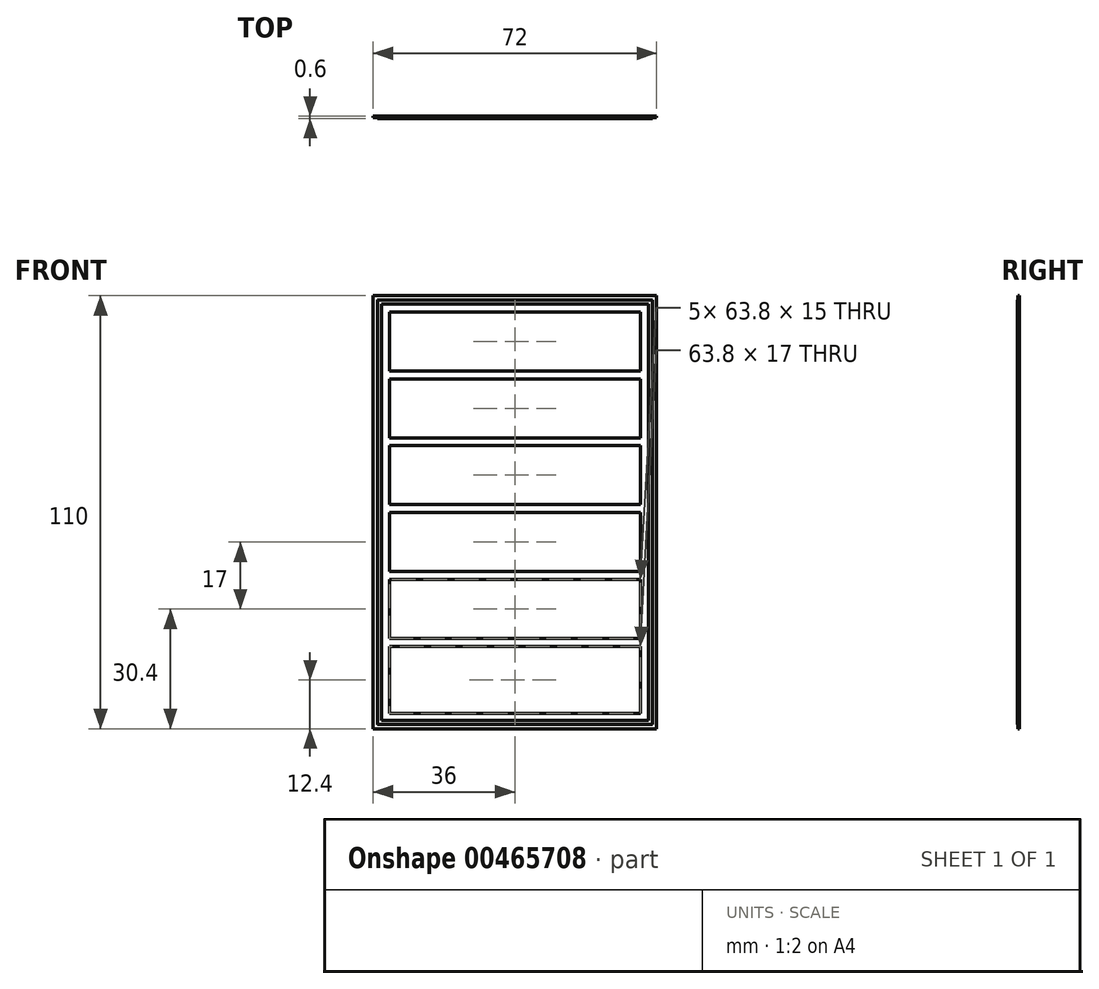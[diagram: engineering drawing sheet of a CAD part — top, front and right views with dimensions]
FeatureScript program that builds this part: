
annotation { "Feature Type Name" : "Feature", "Feature Type Description" : "" }
export const myFeature = defineFeature(function(context is Context, id is Id, definition is map)
    precondition{}
    {
        {
            var Q0;
            Q0=qCreatedBy(makeId("Top.planeOp"),FACE);
            var sketch = newSketch(context, id + "F0", { "sketchPlane" : qUnion([Q0])});
            skLineSegment(sketch, "E0.bottom", {"start": v(36, 0.05) * mm, "end": v(-36, 0.05) * mm});
            skLineSegment(sketch, "E0.top", {"start": v(36, -0.05) * mm, "end": v(-36, -0.05) * mm});
            skLineSegment(sketch, "E0.left", {"start": v(36, 0.05) * mm, "end": v(36, -0.05) * mm});
            skLineSegment(sketch, "E0.right", {"start": v(-36, 0.05) * mm, "end": v(-36, -0.05) * mm});
            skPoint(sketch, "E0.middle", {"position": v(0, 0) * mm});
            skSolve(sketch);
        }
        {
            var Q0;
            Q0 = qSketchRegion(id + "F0", true);
            extrude(context, id + "F1", {"entities" : qUnion([Q0]), "depth" : 110 * mm});
        }
        {
            var Q0;
            Q0=makeQuery(id+"F1.opExtrude","SWEPT_FACE",FACE,{"disambiguationData":[OSD([sQuery(id+"F0.wireOp",EDGE,"E0.top")])]});
            var sketch = newSketch(context, id + "F2", { "sketchPlane" : qUnion([Q0])});
            skPoint(sketch, "E1", {"position": v(-34.9, 1.1) * mm});
            skPoint(sketch, "E2", {"position": v(-34.9, 108.9) * mm});
            skPoint(sketch, "E3", {"position": v(34.9, 108.9) * mm});
            skPoint(sketch, "E4", {"position": v(34.9, 1.1) * mm});
            skLineSegment(sketch, "E5", {"start": v(-34.9, 108.9) * mm, "end": v(34.9, 108.9) * mm});
            skLineSegment(sketch, "E6", {"start": v(34.9, 1.1) * mm, "end": v(-34.9, 1.1) * mm});
            skLineSegment(sketch, "E7", {"start": v(-34.9, 1.1) * mm, "end": v(-34.9, 108.9) * mm});
            skLineSegment(sketch, "E8", {"start": v(34.9, 108.9) * mm, "end": v(34.9, 1.1) * mm});
            skPoint(sketch, "E9", {"position": v(-33.9, 2.1) * mm});
            skLineSegment(sketch, "E10.bottom", {"start": v(-33.9, 2.1) * mm, "end": v(33.9, 2.1) * mm});
            skLineSegment(sketch, "E10.top", {"start": v(-33.9, 107.9) * mm, "end": v(33.9, 107.9) * mm});
            skLineSegment(sketch, "E10.left", {"start": v(-33.9, 2.1) * mm, "end": v(-33.9, 107.9) * mm});
            skLineSegment(sketch, "E10.right", {"start": v(33.9, 2.1) * mm, "end": v(33.9, 107.9) * mm});
            skSolve(sketch);
        }
        {
            var Q0;
            Q0 = qSketchRegion(id + "F2", true);
            extrude(context, id + "F3", {"entities" : qUnion([Q0]), "operationType" : NewBodyOperationType.ADD, "depth" : .25 * mm});
        }
        {
            var Q0;
            Q0=makeQuery(id+"F1.opExtrude","SWEPT_FACE",FACE,{"disambiguationData":[OSD([sQuery(id+"F0.wireOp",EDGE,"E0.bottom")])]});
            var sketch = newSketch(context, id + "F4", { "sketchPlane" : qUnion([Q0])});
            skLineSegment(sketch, "E11.bottom", {"start": v(36, 110) * mm, "end": v(-36, 110) * mm});
            skLineSegment(sketch, "E11.top", {"start": v(36, 0) * mm, "end": v(-36, 0) * mm});
            skLineSegment(sketch, "E11.left", {"start": v(36, 110) * mm, "end": v(36, 0) * mm});
            skLineSegment(sketch, "E11.right", {"start": v(-36, 110) * mm, "end": v(-36, 0) * mm});
            skPoint(sketch, "E12", {"position": v(35, 109) * mm});
            skPoint(sketch, "E13", {"position": v(-35, 1) * mm});
            skLineSegment(sketch, "E14.bottom", {"start": v(-35, 1) * mm, "end": v(35, 1) * mm});
            skLineSegment(sketch, "E14.top", {"start": v(-35, 109) * mm, "end": v(35, 109) * mm});
            skLineSegment(sketch, "E14.left", {"start": v(-35, 1) * mm, "end": v(-35, 109) * mm});
            skLineSegment(sketch, "E14.right", {"start": v(35, 1) * mm, "end": v(35, 109) * mm});
            skSolve(sketch);
        }
        {
            var Q0;
            Q0 = qSketchRegion(id + "F4", true);
            extrude(context, id + "F5", {"entities" : qUnion([Q0]), "operationType" : NewBodyOperationType.ADD, "depth" : .25 * mm});
        }
        {
            var Q0;
            Q0=makeQuery(id+"F3.boolean.opBoolean","SPLIT",FACE,{"disambiguationData":[TD([makeQuery(id+"F3.opExtrude","SWEPT_FACE",FACE,{"disambiguationData":[OSD([sQuery(id+"F2.wireOp",EDGE,"E10.bottom")])]})])],"derivedFrom":makeQuery(id+"F1.opExtrude","SWEPT_FACE",FACE,{"disambiguationData":[OSD([sQuery(id+"F0.wireOp",EDGE,"E0.top")])]})});
            var sketch = newSketch(context, id + "F6", { "sketchPlane" : qUnion([Q0])});
            skPoint(sketch, "E15", {"position": v(-33.9, 107.9) * mm});
            skPoint(sketch, "E16", {"position": v(-31.9, 107.9) * mm});
            skPoint(sketch, "E17", {"position": v(-31.9, 90.9) * mm});
            skPoint(sketch, "E18", {"position": v(-31.9, 88.9) * mm});
            skPoint(sketch, "E19", {"position": v(-31.9, 73.9) * mm});
            skPoint(sketch, "E20", {"position": v(-31.9, 71.9) * mm});
            skPoint(sketch, "E21", {"position": v(-31.9, 56.9) * mm});
            skPoint(sketch, "E22", {"position": v(-31.9, 54.9) * mm});
            skPoint(sketch, "E23", {"position": v(-31.9, 39.9) * mm});
            skPoint(sketch, "E24", {"position": v(-31.9, 37.9) * mm});
            skPoint(sketch, "E25", {"position": v(-31.9, 22.9) * mm});
            skPoint(sketch, "E26", {"position": v(-31.9, 20.9) * mm});
            skPoint(sketch, "E27", {"position": v(-31.9, 3.9) * mm});
            skPoint(sketch, "E28", {"position": v(33.9, 107.9) * mm});
            skPoint(sketch, "E29", {"position": v(31.9, 107.9) * mm});
            skPoint(sketch, "E30", {"position": v(-31.9, 105.9) * mm});
            skPoint(sketch, "E31", {"position": v(31.9, 105.9) * mm});
            skPoint(sketch, "E32", {"position": v(31.9, 88.9) * mm});
            skPoint(sketch, "E33", {"position": v(31.9, 71.9) * mm});
            skPoint(sketch, "E34", {"position": v(31.9, 54.9) * mm});
            skPoint(sketch, "E35", {"position": v(31.9, 37.9) * mm});
            skPoint(sketch, "E36", {"position": v(31.9, 20.9) * mm});
            skLineSegment(sketch, "E37.bottom", {"start": v(-31.9, 90.9) * mm, "end": v(31.9, 90.9) * mm});
            skLineSegment(sketch, "E37.top", {"start": v(-31.9, 105.9) * mm, "end": v(31.9, 105.9) * mm});
            skLineSegment(sketch, "E37.left", {"start": v(-31.9, 90.9) * mm, "end": v(-31.9, 105.9) * mm});
            skLineSegment(sketch, "E37.right", {"start": v(31.9, 90.9) * mm, "end": v(31.9, 105.9) * mm});
            skLineSegment(sketch, "E38.bottom", {"start": v(-31.9, 73.9) * mm, "end": v(31.9, 73.9) * mm});
            skLineSegment(sketch, "E38.top", {"start": v(-31.9, 88.9) * mm, "end": v(31.9, 88.9) * mm});
            skLineSegment(sketch, "E38.left", {"start": v(-31.9, 73.9) * mm, "end": v(-31.9, 88.9) * mm});
            skLineSegment(sketch, "E38.right", {"start": v(31.9, 73.9) * mm, "end": v(31.9, 88.9) * mm});
            skLineSegment(sketch, "E39.bottom", {"start": v(-31.9, 56.9) * mm, "end": v(31.9, 56.9) * mm});
            skLineSegment(sketch, "E39.top", {"start": v(-31.9, 71.9) * mm, "end": v(31.9, 71.9) * mm});
            skLineSegment(sketch, "E39.left", {"start": v(-31.9, 56.9) * mm, "end": v(-31.9, 71.9) * mm});
            skLineSegment(sketch, "E39.right", {"start": v(31.9, 56.9) * mm, "end": v(31.9, 71.9) * mm});
            skLineSegment(sketch, "E40.bottom", {"start": v(-31.9, 39.9) * mm, "end": v(31.9, 39.9) * mm});
            skLineSegment(sketch, "E40.top", {"start": v(-31.9, 54.9) * mm, "end": v(31.9, 54.9) * mm});
            skLineSegment(sketch, "E40.left", {"start": v(-31.9, 39.9) * mm, "end": v(-31.9, 54.9) * mm});
            skLineSegment(sketch, "E40.right", {"start": v(31.9, 39.9) * mm, "end": v(31.9, 54.9) * mm});
            skLineSegment(sketch, "E41.bottom", {"start": v(-31.9, 22.9) * mm, "end": v(31.9, 22.9) * mm});
            skLineSegment(sketch, "E41.top", {"start": v(-31.9, 37.9) * mm, "end": v(31.9, 37.9) * mm});
            skLineSegment(sketch, "E41.left", {"start": v(-31.9, 22.9) * mm, "end": v(-31.9, 37.9) * mm});
            skLineSegment(sketch, "E41.right", {"start": v(31.9, 22.9) * mm, "end": v(31.9, 37.9) * mm});
            skLineSegment(sketch, "E42.bottom", {"start": v(-31.9, 3.9) * mm, "end": v(31.9, 3.9) * mm});
            skLineSegment(sketch, "E42.top", {"start": v(-31.9, 20.9) * mm, "end": v(31.9, 20.9) * mm});
            skLineSegment(sketch, "E42.left", {"start": v(-31.9, 3.9) * mm, "end": v(-31.9, 20.9) * mm});
            skLineSegment(sketch, "E42.right", {"start": v(31.9, 3.9) * mm, "end": v(31.9, 20.9) * mm});
            skSolve(sketch);
        }
        {
            var Q0;
            Q0 = qSketchRegion(id + "F6", true);
            extrude(context, id + "F7", {"entities" : qUnion([Q0]), "operationType" : NewBodyOperationType.REMOVE, "oppositeDirection" : true, "depth" : 2 * mm});
        }
    });
